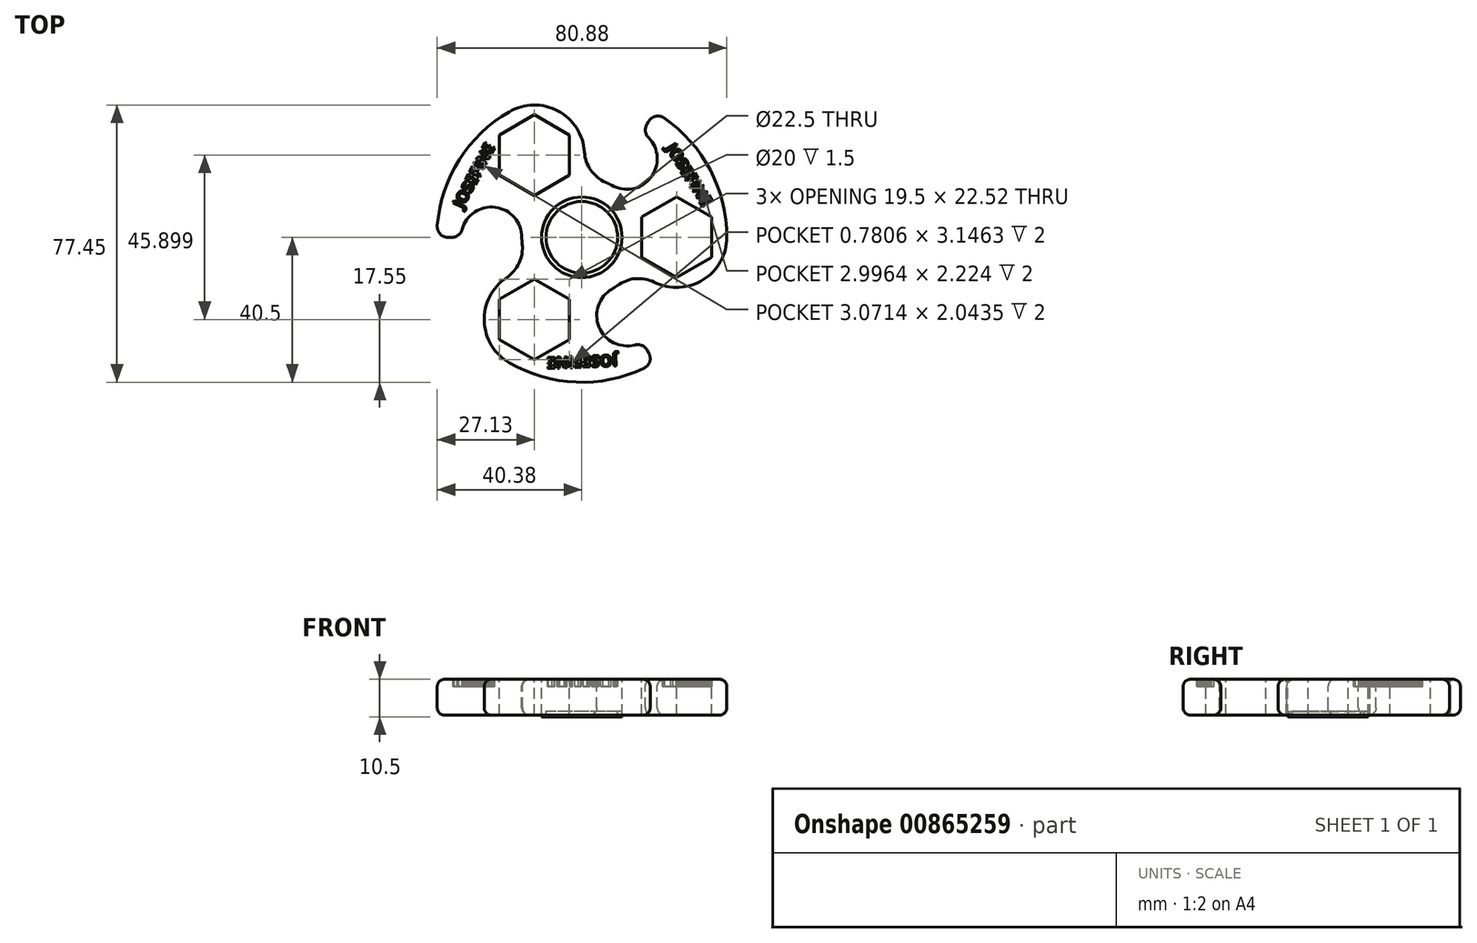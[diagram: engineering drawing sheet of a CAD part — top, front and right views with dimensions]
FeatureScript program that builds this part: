
annotation { "Feature Type Name" : "Feature", "Feature Type Description" : "" }
export const myFeature = defineFeature(function(context is Context, id is Id, definition is map)
    precondition{}
    {
        {
            var Q0;
            Q0=qCreatedBy(makeId("Top.planeOp"),FACE);
            var sketch = newSketch(context, id + "F0", { "sketchPlane" : qUnion([Q0])});
            skCircle(sketch, "E0", {"center": v(0, 0) * mm, "radius": 11.25 * mm});
            skCircle(sketch, "E1.cCircle", {"center": v(26.5, 0) * mm, "radius": 9.75 * mm, "construction": true});
            skLineSegment(sketch, "E1.0", {"start": v(36.25, 5.63) * mm, "end": v(36.25, -5.63) * mm});
            skLineSegment(sketch, "E1.1", {"start": v(36.25, -5.63) * mm, "end": v(26.5, -11.26) * mm});
            skLineSegment(sketch, "E1.2", {"start": v(26.5, -11.26) * mm, "end": v(16.75, -5.63) * mm});
            skLineSegment(sketch, "E1.3", {"start": v(16.75, -5.63) * mm, "end": v(16.75, 5.63) * mm});
            skLineSegment(sketch, "E1.4", {"start": v(16.75, 5.63) * mm, "end": v(26.5, 11.26) * mm});
            skLineSegment(sketch, "E1.5", {"start": v(26.5, 11.26) * mm, "end": v(36.25, 5.63) * mm});
            skPoint(sketch, "E1.0.midPoint", {"position": v(9.75, 0) * mm});
            skLineSegment(sketch, "E2", {"start": v(26.5, 11.26) * mm, "end": v(16.75, 5.63) * mm});
            skLineSegment(sketch, "E3", {"start": v(16.75, 5.63) * mm, "end": v(16.75, -5.63) * mm});
            skLineSegment(sketch, "E4", {"start": v(16.75, -5.63) * mm, "end": v(26.5, -11.26) * mm});
            skLineSegment(sketch, "E5", {"start": v(26.5, -11.26) * mm, "end": v(36.25, -5.63) * mm});
            skLineSegment(sketch, "E6", {"start": v(36.25, -5.63) * mm, "end": v(36.25, 5.63) * mm});
            skLineSegment(sketch, "E7", {"start": v(36.25, 5.63) * mm, "end": v(26.5, 11.26) * mm});
            skArc(sketch, "E8", {"start": v(8.38, 14.5) * mm, "mid": v(7.55, 14.95) * mm, "end": v(6.7, 15.35) * mm});
            skArc(sketch, "E9", {"start": v(20.3, -12.56) * mm, "mid": v(33.9, -11.89) * mm, "end": v(40.5, 0) * mm});
            skArc(sketch, "E10", {"start": v(40.5, 0) * mm, "mid": v(35.85, 18.84) * mm, "end": v(22.97, 33.35) * mm});
            skLineSegment(sketch, "E11", {"start": v(8.32, 14.54) * mm, "end": v(8.32, 14.54) * mm});
            skArc(sketch, "E12", {"start": v(8.32, 14.54) * mm, "mid": v(19.3, 16.7) * mm, "end": v(18.62, 27.87) * mm});
            skLineSegment(sketch, "E13", {"start": v(0, 0) * mm, "end": v(44.66, 0) * mm});
            skLineSegment(sketch, "E14.trimOffspring", {"start": v(18.16, 31.5) * mm, "end": v(18.68, 32.39) * mm});
            skPoint(sketch, "E15.visualSharp", {"position": v(14.85, -7.76) * mm});
            skArc(sketch, "E15.filletArc", {"start": v(20.3, -12.56) * mm, "mid": v(15, -11.56) * mm, "end": v(9.95, -13.48) * mm});
            skPoint(sketch, "E16.visualSharp", {"position": v(20.24, 35.08) * mm});
            skArc(sketch, "E16.filletArc", {"start": v(22.97, 33.35) * mm, "mid": v(20.62, 33.8) * mm, "end": v(18.68, 32.39) * mm});
            skPoint(sketch, "E17.visualSharp", {"position": v(16.85, 29.24) * mm});
            skArc(sketch, "E17.filletArc", {"start": v(18.16, 31.5) * mm, "mid": v(17.78, 29.6) * mm, "end": v(18.62, 27.87) * mm});
            skArc(sketch, "E18.1.0", {"start": v(-16.75, -0.07) * mm, "mid": v(-24.11, 8.38) * mm, "end": v(-33.45, 2.19) * mm});
            skArc(sketch, "E18.1.1", {"start": v(-36.35, -0.02) * mm, "mid": v(-34.53, 0.6) * mm, "end": v(-33.45, 2.19) * mm});
            skLineSegment(sketch, "E18.1.2", {"start": v(-36.35, -0.02) * mm, "end": v(-37.39, -0.02) * mm});
            skArc(sketch, "E18.1.3", {"start": v(-40.37, 3.22) * mm, "mid": v(-39.59, 0.95) * mm, "end": v(-37.39, -0.02) * mm});
            skArc(sketch, "E18.1.4", {"start": v(-20.25, 35.07) * mm, "mid": v(-34.24, 21.63) * mm, "end": v(-40.37, 3.22) * mm});
            skArc(sketch, "E18.1.5", {"start": v(0.72, 23.86) * mm, "mid": v(-6.65, 35.3) * mm, "end": v(-20.25, 35.07) * mm});
            skArc(sketch, "E18.1.6", {"start": v(0.72, 23.86) * mm, "mid": v(2.52, 18.77) * mm, "end": v(6.7, 15.35) * mm});
            skLineSegment(sketch, "E18.1.7", {"start": v(-3.5, 17.32) * mm, "end": v(-3.5, 28.58) * mm});
            skLineSegment(sketch, "E18.1.8", {"start": v(-3.5, 28.58) * mm, "end": v(-13.25, 34.2) * mm});
            skLineSegment(sketch, "E18.1.9", {"start": v(-13.25, 34.2) * mm, "end": v(-23, 28.58) * mm});
            skLineSegment(sketch, "E18.1.10", {"start": v(-23, 28.58) * mm, "end": v(-23, 17.32) * mm});
            skLineSegment(sketch, "E18.1.11", {"start": v(-23, 17.32) * mm, "end": v(-13.25, 11.7) * mm});
            skLineSegment(sketch, "E18.1.12", {"start": v(-13.25, 11.7) * mm, "end": v(-3.5, 17.32) * mm});
            skArc(sketch, "E18.2.0", {"start": v(8.43, -14.47) * mm, "mid": v(4.8, -25.07) * mm, "end": v(14.83, -30.06) * mm});
            skArc(sketch, "E18.2.1", {"start": v(18.2, -31.47) * mm, "mid": v(16.75, -30.2) * mm, "end": v(14.83, -30.06) * mm});
            skLineSegment(sketch, "E18.2.2", {"start": v(18.2, -31.47) * mm, "end": v(18.71, -32.37) * mm});
            skArc(sketch, "E18.2.3", {"start": v(17.4, -36.57) * mm, "mid": v(18.97, -34.76) * mm, "end": v(18.71, -32.37) * mm});
            skArc(sketch, "E18.2.4", {"start": v(-20.25, -35.07) * mm, "mid": v(-1.61, -40.47) * mm, "end": v(17.4, -36.57) * mm});
            skArc(sketch, "E18.2.5", {"start": v(-21.03, -11.3) * mm, "mid": v(-27.24, -23.4) * mm, "end": v(-20.25, -35.07) * mm});
            skArc(sketch, "E18.2.6", {"start": v(-21.03, -11.3) * mm, "mid": v(-17.51, -7.2) * mm, "end": v(-16.64, -1.87) * mm});
            skLineSegment(sketch, "E18.2.7", {"start": v(-13.25, -11.7) * mm, "end": v(-23, -17.32) * mm});
            skLineSegment(sketch, "E18.2.8", {"start": v(-23, -17.32) * mm, "end": v(-23, -28.58) * mm});
            skLineSegment(sketch, "E18.2.9", {"start": v(-23, -28.58) * mm, "end": v(-13.25, -34.2) * mm});
            skLineSegment(sketch, "E18.2.10", {"start": v(-13.25, -34.2) * mm, "end": v(-3.5, -28.58) * mm});
            skLineSegment(sketch, "E18.2.11", {"start": v(-3.5, -28.58) * mm, "end": v(-3.5, -17.32) * mm});
            skLineSegment(sketch, "E18.2.12", {"start": v(-3.5, -17.32) * mm, "end": v(-13.25, -11.7) * mm});
            skArc(sketch, "E19.trimOffspring", {"start": v(-16.75, 0) * mm, "mid": v(-16.72, -0.94) * mm, "end": v(-16.64, -1.87) * mm});
            skArc(sketch, "E20.trimOffspring", {"start": v(8.37, -14.5) * mm, "mid": v(9.17, -14.02) * mm, "end": v(9.95, -13.48) * mm});
            skSolve(sketch);
        }
        {
            var Q0;
            Q0=qCreatedBy(makeId("Top.planeOp"),FACE);
            cPlane(context, id + "F1", {"entities" : qUnion([Q0]), "cplaneType" : CPlaneType.OFFSET, "offset" : 5 * mm, "width" : 150 * mm, "height" : 150 * mm});
        }
        {
            var Q0;
            Q0=qCreatedBy(id+"F1.planeOp",FACE);
            var sketch = newSketch(context, id + "F2", { "sketchPlane" : qUnion([Q0])});
            skText(sketch, "E21", { "text": "JOSEFINE", "fontName": "OpenSans-Bold.ttf"});
            const initialGuessF2  = {"E21": [0.02348, 0.02495, 0.53257, -0.84639, 0.00315]};
            skSetInitialGuess(sketch, initialGuessF2);
            skSolve(sketch);
        }
        {
            var Q0;
            Q0=qCreatedBy(makeId("Top.planeOp"),FACE);
            var sketch = newSketch(context, id + "F3", { "sketchPlane" : qUnion([Q0])});
            skCircle(sketch, "E22", {"center": v(0, 0) * mm, "radius": 11.25 * mm});
            skCircle(sketch, "E23", {"center": v(0, 0) * mm, "radius": 10 * mm});
            skSolve(sketch);
        }
        {
            var Q0;
            Q0=makeQuery(id+"F0.imprint","IMPRINT",FACE,{"disambiguationData":[TD([[makeQuery(id+"F0.imprint","IMPRINT",EDGE,{"derivedFrom":sQuery(id+"F0.wireOp",EDGE,"E0")}),-1.0]])]});
            extrude(context, id + "F4", {"entities" : qUnion([Q0]), "depth" : -10 * mm, "offsetDistance" : 25 * mm});
        }
        {
            var Q0;
            Q0=makeQuery(id+"F3.imprint","IMPRINT",FACE,{"disambiguationData":[TD([[makeQuery(id+"F3.imprint","IMPRINT",EDGE,{"derivedFrom":sQuery(id+"F3.wireOp",EDGE,"E22")}),1.0]])]});
            extrude(context, id + "F5", {"entities" : qUnion([Q0]), "depth" : -1.5 * mm, "offsetDistance" : 25 * mm});
        }
        {
            var Q0;
            Q0=qSketchRegion(id+"F2",true);
            extrude(context, id + "F6", {"entities" : qUnion([Q0]), "depth" : -7 * mm, "offsetDistance" : 25 * mm});
        }
        {
            var Q0;
            Q0=makeQuery(id+"F4.opExtrude","CAP_EDGE",EDGE,{"disambiguationData":[OSD([sQuery(id+"F0.wireOp",EDGE,"E18.1.4")])],"isStart":true});
            var Q1;
            Q1=makeQuery(id+"F4.opExtrude","CAP_EDGE",EDGE,{"disambiguationData":[OSD([sQuery(id+"F0.wireOp",EDGE,"E18.1.5")])],"isStart":true});
            var Q2;
            Q2=makeQuery(id+"F4.opExtrude","CAP_EDGE",EDGE,{"disambiguationData":[OSD([sQuery(id+"F0.wireOp",EDGE,"E12")])],"isStart":true});
            var Q3;
            Q3=makeQuery(id+"F4.opExtrude","CAP_EDGE",EDGE,{"disambiguationData":[OSD([sQuery(id+"F0.wireOp",EDGE,"E18.2.2")])],"isStart":true});
            fillet(context, id + "F7", {"entities" : qUnion([Q0, Q1, Q2, Q3]), "radius" : 2 * mm, "tangentPropagation" : true, "allowEdgeOverflow" : false});
        }
        {
            var Q0;
            Q0=makeQuery(id+"F4.opExtrude","CAP_EDGE",EDGE,{"disambiguationData":[OSD([sQuery(id+"F0.wireOp",EDGE,"E18.2.4")])],"isStart":false});
            var Q1;
            Q1=makeQuery(id+"F4.opExtrude","CAP_EDGE",EDGE,{"disambiguationData":[OSD([sQuery(id+"F0.wireOp",EDGE,"E18.2.3")])],"isStart":false});
            var Q2;
            Q2=makeQuery(id+"F4.opExtrude","CAP_EDGE",EDGE,{"disambiguationData":[OSD([sQuery(id+"F0.wireOp",EDGE,"E9")])],"isStart":false});
            var Q3;
            Q3=makeQuery(id+"F4.opExtrude","CAP_EDGE",EDGE,{"disambiguationData":[OSD([sQuery(id+"F0.wireOp",EDGE,"E18.1.5")])],"isStart":false});
            fillet(context, id + "F8", {"entities" : qUnion([Q0, Q1, Q2, Q3]), "radius" : 2 * mm, "tangentPropagation" : true, "allowEdgeOverflow" : false});
        }
        {
            var Q0;
            Q0=makeQuery(id+"F6.opExtrude","SWEPT_BODY",BODY,{"disambiguationData":[OSD([sQuery(id+"F2.wireOp",EDGE,"E21.sketch_text.stroke-10"),sQuery(id+"F2.wireOp",EDGE,"E21.sketch_text.stroke-11"),sQuery(id+"F2.wireOp",EDGE,"E21.sketch_text.stroke-12"),sQuery(id+"F2.wireOp",EDGE,"E21.sketch_text.stroke-13"),sQuery(id+"F2.wireOp",EDGE,"E21.sketch_text.stroke-14"),sQuery(id+"F2.wireOp",EDGE,"E21.sketch_text.stroke-15"),sQuery(id+"F2.wireOp",EDGE,"E21.sketch_text.stroke-16"),sQuery(id+"F2.wireOp",EDGE,"E21.sketch_text.stroke-17"),sQuery(id+"F2.wireOp",EDGE,"E21.sketch_text.stroke-18"),sQuery(id+"F2.wireOp",EDGE,"E21.sketch_text.stroke-19"),sQuery(id+"F2.wireOp",EDGE,"E21.sketch_text.stroke-20"),sQuery(id+"F2.wireOp",EDGE,"E21.sketch_text.stroke-21"),sQuery(id+"F2.wireOp",EDGE,"E21.sketch_text.stroke-22"),sQuery(id+"F2.wireOp",EDGE,"E21.sketch_text.stroke-23")])]});
            var Q1;
            Q1=makeQuery(id+"F6.opExtrude","SWEPT_BODY",BODY,{"disambiguationData":[OSD([sQuery(id+"F2.wireOp",EDGE,"E21.sketch_text.stroke-0"),sQuery(id+"F2.wireOp",EDGE,"E21.sketch_text.stroke-1"),sQuery(id+"F2.wireOp",EDGE,"E21.sketch_text.stroke-2"),sQuery(id+"F2.wireOp",EDGE,"E21.sketch_text.stroke-3"),sQuery(id+"F2.wireOp",EDGE,"E21.sketch_text.stroke-4"),sQuery(id+"F2.wireOp",EDGE,"E21.sketch_text.stroke-5"),sQuery(id+"F2.wireOp",EDGE,"E21.sketch_text.stroke-6"),sQuery(id+"F2.wireOp",EDGE,"E21.sketch_text.stroke-7"),sQuery(id+"F2.wireOp",EDGE,"E21.sketch_text.stroke-8"),sQuery(id+"F2.wireOp",EDGE,"E21.sketch_text.stroke-9")])]});
            var Q2;
            Q2=makeQuery(id+"F6.opExtrude","SWEPT_BODY",BODY,{"disambiguationData":[OSD([sQuery(id+"F2.wireOp",EDGE,"E21.sketch_text.stroke-24"),sQuery(id+"F2.wireOp",EDGE,"E21.sketch_text.stroke-25"),sQuery(id+"F2.wireOp",EDGE,"E21.sketch_text.stroke-26"),sQuery(id+"F2.wireOp",EDGE,"E21.sketch_text.stroke-27"),sQuery(id+"F2.wireOp",EDGE,"E21.sketch_text.stroke-28"),sQuery(id+"F2.wireOp",EDGE,"E21.sketch_text.stroke-29"),sQuery(id+"F2.wireOp",EDGE,"E21.sketch_text.stroke-30"),sQuery(id+"F2.wireOp",EDGE,"E21.sketch_text.stroke-31"),sQuery(id+"F2.wireOp",EDGE,"E21.sketch_text.stroke-32"),sQuery(id+"F2.wireOp",EDGE,"E21.sketch_text.stroke-33"),sQuery(id+"F2.wireOp",EDGE,"E21.sketch_text.stroke-34"),sQuery(id+"F2.wireOp",EDGE,"E21.sketch_text.stroke-35"),sQuery(id+"F2.wireOp",EDGE,"E21.sketch_text.stroke-36"),sQuery(id+"F2.wireOp",EDGE,"E21.sketch_text.stroke-37"),sQuery(id+"F2.wireOp",EDGE,"E21.sketch_text.stroke-38"),sQuery(id+"F2.wireOp",EDGE,"E21.sketch_text.stroke-39"),sQuery(id+"F2.wireOp",EDGE,"E21.sketch_text.stroke-40"),sQuery(id+"F2.wireOp",EDGE,"E21.sketch_text.stroke-41"),sQuery(id+"F2.wireOp",EDGE,"E21.sketch_text.stroke-42"),sQuery(id+"F2.wireOp",EDGE,"E21.sketch_text.stroke-43"),sQuery(id+"F2.wireOp",EDGE,"E21.sketch_text.stroke-44"),sQuery(id+"F2.wireOp",EDGE,"E21.sketch_text.stroke-45"),sQuery(id+"F2.wireOp",EDGE,"E21.sketch_text.stroke-46"),sQuery(id+"F2.wireOp",EDGE,"E21.sketch_text.stroke-47"),sQuery(id+"F2.wireOp",EDGE,"E21.sketch_text.stroke-48"),sQuery(id+"F2.wireOp",EDGE,"E21.sketch_text.stroke-49"),sQuery(id+"F2.wireOp",EDGE,"E21.sketch_text.stroke-50"),sQuery(id+"F2.wireOp",EDGE,"E21.sketch_text.stroke-51")])]});
            var Q3;
            Q3=makeQuery(id+"F6.opExtrude","SWEPT_BODY",BODY,{"disambiguationData":[OSD([sQuery(id+"F2.wireOp",EDGE,"E21.sketch_text.stroke-52"),sQuery(id+"F2.wireOp",EDGE,"E21.sketch_text.stroke-53"),sQuery(id+"F2.wireOp",EDGE,"E21.sketch_text.stroke-54"),sQuery(id+"F2.wireOp",EDGE,"E21.sketch_text.stroke-55"),sQuery(id+"F2.wireOp",EDGE,"E21.sketch_text.stroke-56"),sQuery(id+"F2.wireOp",EDGE,"E21.sketch_text.stroke-57"),sQuery(id+"F2.wireOp",EDGE,"E21.sketch_text.stroke-58"),sQuery(id+"F2.wireOp",EDGE,"E21.sketch_text.stroke-59"),sQuery(id+"F2.wireOp",EDGE,"E21.sketch_text.stroke-60"),sQuery(id+"F2.wireOp",EDGE,"E21.sketch_text.stroke-61"),sQuery(id+"F2.wireOp",EDGE,"E21.sketch_text.stroke-62"),sQuery(id+"F2.wireOp",EDGE,"E21.sketch_text.stroke-63")])]});
            var Q4;
            Q4=makeQuery(id+"F6.opExtrude","SWEPT_BODY",BODY,{"disambiguationData":[OSD([sQuery(id+"F2.wireOp",EDGE,"E21.sketch_text.stroke-64"),sQuery(id+"F2.wireOp",EDGE,"E21.sketch_text.stroke-65"),sQuery(id+"F2.wireOp",EDGE,"E21.sketch_text.stroke-66"),sQuery(id+"F2.wireOp",EDGE,"E21.sketch_text.stroke-67"),sQuery(id+"F2.wireOp",EDGE,"E21.sketch_text.stroke-68"),sQuery(id+"F2.wireOp",EDGE,"E21.sketch_text.stroke-69"),sQuery(id+"F2.wireOp",EDGE,"E21.sketch_text.stroke-70"),sQuery(id+"F2.wireOp",EDGE,"E21.sketch_text.stroke-71"),sQuery(id+"F2.wireOp",EDGE,"E21.sketch_text.stroke-72"),sQuery(id+"F2.wireOp",EDGE,"E21.sketch_text.stroke-73")])]});
            var Q5;
            Q5=makeQuery(id+"F6.opExtrude","SWEPT_BODY",BODY,{"disambiguationData":[OSD([sQuery(id+"F2.wireOp",EDGE,"E21.sketch_text.stroke-74"),sQuery(id+"F2.wireOp",EDGE,"E21.sketch_text.stroke-75"),sQuery(id+"F2.wireOp",EDGE,"E21.sketch_text.stroke-76"),sQuery(id+"F2.wireOp",EDGE,"E21.sketch_text.stroke-77")])]});
            var Q6;
            Q6=makeQuery(id+"F6.opExtrude","SWEPT_BODY",BODY,{"disambiguationData":[OSD([sQuery(id+"F2.wireOp",EDGE,"E21.sketch_text.stroke-78"),sQuery(id+"F2.wireOp",EDGE,"E21.sketch_text.stroke-79"),sQuery(id+"F2.wireOp",EDGE,"E21.sketch_text.stroke-80"),sQuery(id+"F2.wireOp",EDGE,"E21.sketch_text.stroke-81"),sQuery(id+"F2.wireOp",EDGE,"E21.sketch_text.stroke-82"),sQuery(id+"F2.wireOp",EDGE,"E21.sketch_text.stroke-83"),sQuery(id+"F2.wireOp",EDGE,"E21.sketch_text.stroke-84"),sQuery(id+"F2.wireOp",EDGE,"E21.sketch_text.stroke-85"),sQuery(id+"F2.wireOp",EDGE,"E21.sketch_text.stroke-86"),sQuery(id+"F2.wireOp",EDGE,"E21.sketch_text.stroke-87"),sQuery(id+"F2.wireOp",EDGE,"E21.sketch_text.stroke-88"),sQuery(id+"F2.wireOp",EDGE,"E21.sketch_text.stroke-89"),sQuery(id+"F2.wireOp",EDGE,"E21.sketch_text.stroke-90"),sQuery(id+"F2.wireOp",EDGE,"E21.sketch_text.stroke-91")])]});
            var Q7;
            Q7=makeQuery(id+"F6.opExtrude","SWEPT_BODY",BODY,{"disambiguationData":[OSD([sQuery(id+"F2.wireOp",EDGE,"E21.sketch_text.stroke-92"),sQuery(id+"F2.wireOp",EDGE,"E21.sketch_text.stroke-93"),sQuery(id+"F2.wireOp",EDGE,"E21.sketch_text.stroke-94"),sQuery(id+"F2.wireOp",EDGE,"E21.sketch_text.stroke-95"),sQuery(id+"F2.wireOp",EDGE,"E21.sketch_text.stroke-96"),sQuery(id+"F2.wireOp",EDGE,"E21.sketch_text.stroke-97"),sQuery(id+"F2.wireOp",EDGE,"E21.sketch_text.stroke-98"),sQuery(id+"F2.wireOp",EDGE,"E21.sketch_text.stroke-99"),sQuery(id+"F2.wireOp",EDGE,"E21.sketch_text.stroke-100"),sQuery(id+"F2.wireOp",EDGE,"E21.sketch_text.stroke-101"),sQuery(id+"F2.wireOp",EDGE,"E21.sketch_text.stroke-102"),sQuery(id+"F2.wireOp",EDGE,"E21.sketch_text.stroke-103")])]});
            var Q8;
            Q8=makeQuery(id+"F5.opExtrude","CAP_EDGE",EDGE,{"disambiguationData":[OSD([sQuery(id+"F3.wireOp",EDGE,"E23")])],"isStart":true});
            circularPattern(context, id + "F9", {"operationType" : NewBodyOperationType.REMOVE, "entities" : qUnion([Q0, Q1, Q2, Q3, Q4, Q5, Q6, Q7]), "axis" : qUnion([Q8]), "angle" : 360 * degree, "instanceCount" : 3, "equalSpace" : true, "computeTransformsWithoutBuiltin" : true});
        }
        {
            var Q0;
            Q0=makeQuery(id+"F5.opExtrude","SWEPT_BODY",BODY,{"disambiguationData":[OSD([sQuery(id+"F3.wireOp",EDGE,"E22"),sQuery(id+"F3.wireOp",EDGE,"E23")])]});
            transform(context, id + "F10", {"entities" : qUnion([Q0]), "transformType" : TransformType.TRANSLATION_3D, "dx" : 0 * mm, "dy" : 0 * mm, "dz" : -9 * mm, "makeCopy" : false});
        }
    });
